# Revit family: Sanitary_Showers_AXOR_45771XXX-AXOR-One-Shut-off-valve-for-con_NEW
name_source: partatom
category: Plumbing Fixtures
revit_build: Autodesk Revit 2018 (Build: 20170223_1515(x64)
units: mm (PartAtom-declared; Revit-internal decimal feet)

## family parameters
Always vertical = No
Cut with Voids When Loaded = No
OmniClass Number = 23.27.31.00
OmniClass Title = Valves
Part Type = Normal
Room Calculation Point = No
Round Connector Dimension = Use Diameter
Shared = No
Work Plane-Based = Yes

## types (1)
- Default - please load Revit Family Type Catalog
    Always visible = Yes
    BIMobject category = Showers
    Date of publishing = 9/28/2022 12:00:00 AM
    Default Elevation = 1219.2 mm  [stored 4 ft]
    Description = AXOR One Shut-off valve for concealed installation
    Design country = Germany
    EAN code = 4059625469057
    Edition number = 1
    GTIN code = https://4059625469057
    IFC Classification = Sanitary Terminal
    Manufacturer = AXOR
    Manufacturer country = Germany
    Manufacturer name = AXOR
    Material 1 = AXOR - Metal - 000 Chrome
    Model = 45771XXX
    OmniClass Code = 23-27 31 00
    OmniClass Description = Valves
    Product Guid = df0dab6b-307a-472d-afa4-66dae65123c5
    Product SKU = 45771XXX
    Product data url = https://bimobject.com
    Product family = AXOR One
    Product group = Shut-off valves
    Product name = 45771XXX AXOR One Shut-off valve for concealed installation
    Product url = https://www.axor-design.com
    QR code = https://bimobject.com
    UNSPSC Code = 40141616
    URL = https://www.axor-design.com
    Uniclass 2015 Code = Pr_40_20_87
    Uniclass 2015 Name = Taps and water supply outlet fittings
    Weight Net (Kg) = 1.1

note: [stored X ft] marks values corroborated as IEEE doubles in the binary element streams (Revit-internal decimal feet)

## geometry (parser evidence)
native form markers: Sweep x3
no freeform markers — native parametric forms only
